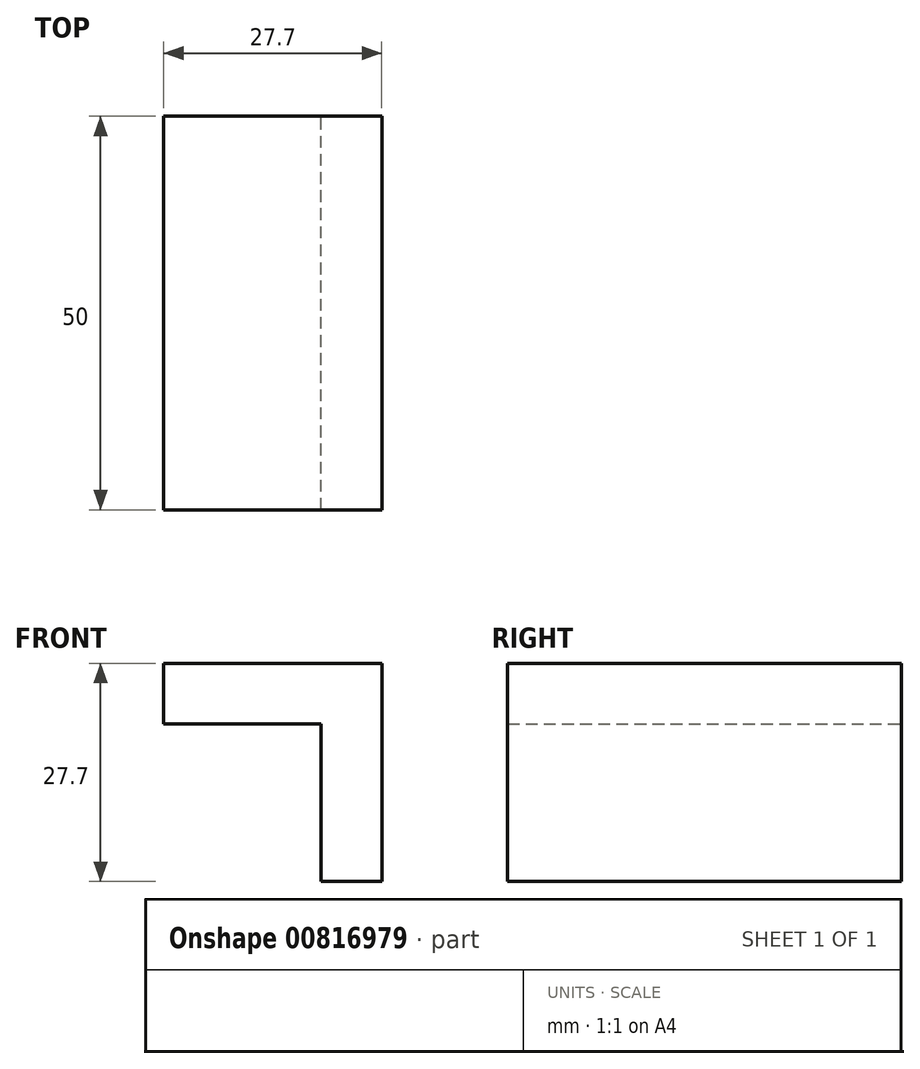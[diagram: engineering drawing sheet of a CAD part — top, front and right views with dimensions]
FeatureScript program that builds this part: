
annotation { "Feature Type Name" : "Feature", "Feature Type Description" : "" }
export const myFeature = defineFeature(function(context is Context, id is Id, definition is map)
    precondition{}
    {
        {
            var Q0;
            Q0=qCreatedBy(makeId("Front.planeOp"),FACE);
            var sketch = newSketch(context, id + "F0", { "sketchPlane" : qUnion([Q0])});
            skLineSegment(sketch, "E0", {"start": v(-20, 0) * mm, "end": v(0, 0) * mm});
            skLineSegment(sketch, "E1", {"start": v(0, 0) * mm, "end": v(0, -20) * mm});
            skLineSegment(sketch, "E2", {"start": v(0, -20) * mm, "end": v(7.7, -20) * mm});
            skLineSegment(sketch, "E3", {"start": v(7.7, -20) * mm, "end": v(7.7, 7.7) * mm});
            skLineSegment(sketch, "E4", {"start": v(7.7, 7.7) * mm, "end": v(-20, 7.7) * mm});
            skLineSegment(sketch, "E5", {"start": v(-20, 7.7) * mm, "end": v(-20, 0) * mm});
            skSolve(sketch);
        }
        {
            var Q0;
            Q0=makeQuery(id+"F0.imprint","IMPRINT",FACE,{"disambiguationData":[TD([[makeQuery(id+"F0.imprint","IMPRINT",EDGE,{"derivedFrom":sQuery(id+"F0.wireOp",EDGE,"E0")}),1.0]])]});
            extrude(context, id + "F1", {"entities" : qUnion([Q0]), "endBound" : BoundingType.SYMMETRIC, "depth" : 50 * mm, "offsetDistance" : 25 * mm});
        }
    });
